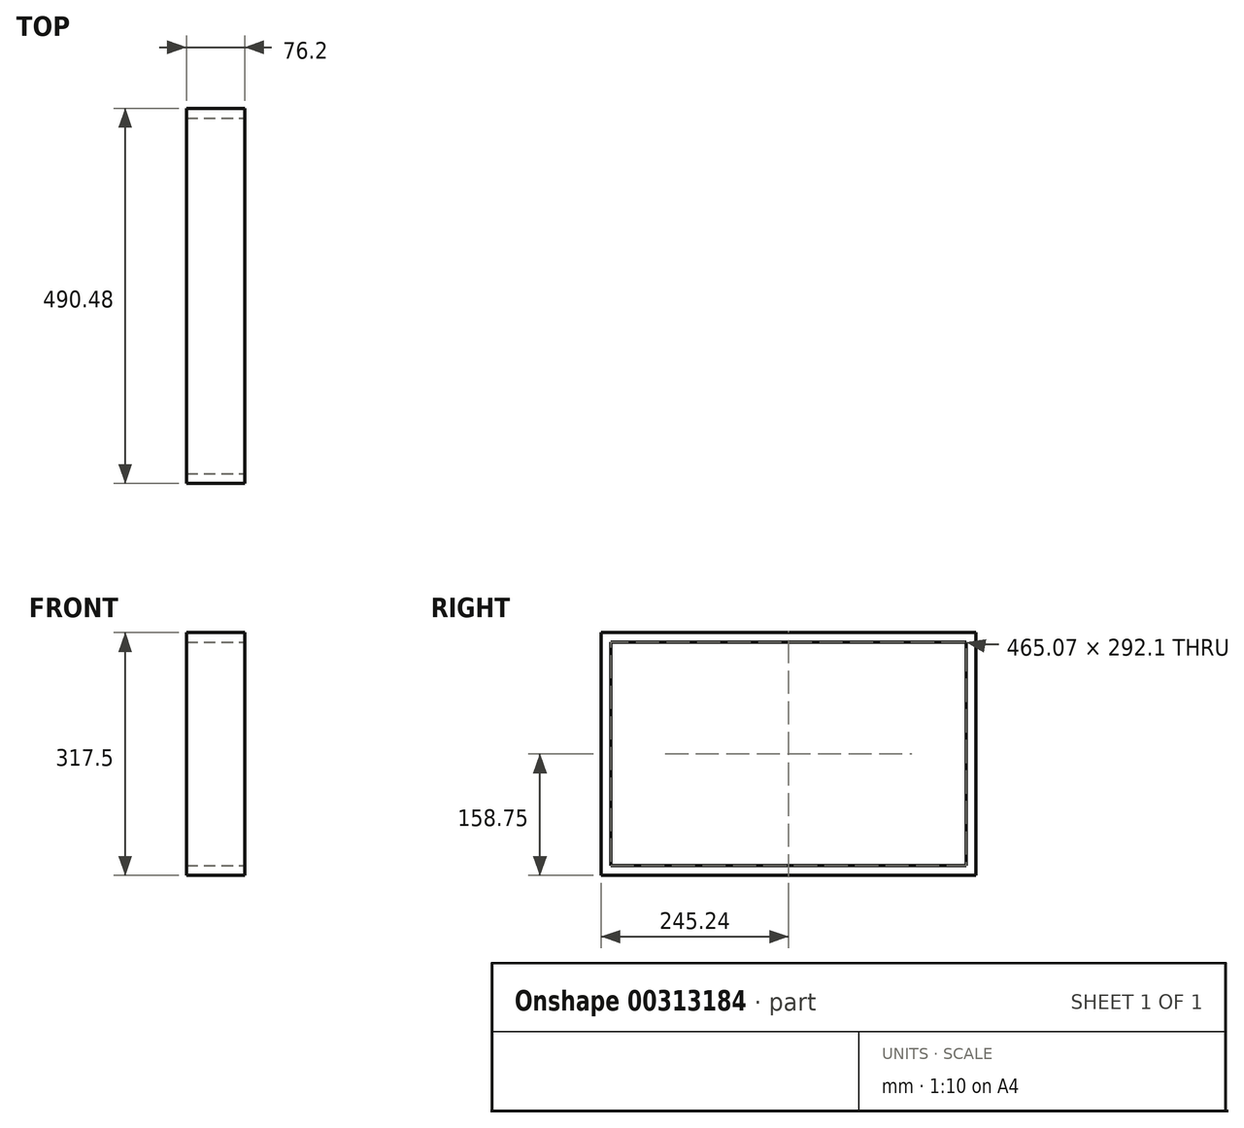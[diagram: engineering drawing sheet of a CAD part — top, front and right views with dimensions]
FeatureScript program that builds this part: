
annotation { "Feature Type Name" : "Feature", "Feature Type Description" : "" }
export const myFeature = defineFeature(function(context is Context, id is Id, definition is map)
    precondition{}
    {
        {
            var Q0;
            Q0=qCreatedBy(makeId("Right.planeOp"),FACE);
            var sketch = newSketch(context, id + "F0", { "sketchPlane" : qUnion([Q0])});
            skLineSegment(sketch, "E0.bottom", {"start": v(245.24, 158.75) * mm, "end": v(-245.24, 158.75) * mm});
            skLineSegment(sketch, "E0.top", {"start": v(245.24, -158.75) * mm, "end": v(-245.24, -158.75) * mm});
            skLineSegment(sketch, "E0.left", {"start": v(245.24, 158.75) * mm, "end": v(245.24, -158.75) * mm});
            skLineSegment(sketch, "E0.right", {"start": v(-245.24, 158.75) * mm, "end": v(-245.24, -158.75) * mm});
            skPoint(sketch, "E0.middle", {"position": v(0, 0) * mm});
            skLineSegment(sketch, "E1.bottom", {"start": v(232.54, 146.05) * mm, "end": v(-232.54, 146.05) * mm});
            skLineSegment(sketch, "E1.top", {"start": v(232.54, -146.05) * mm, "end": v(-232.54, -146.05) * mm});
            skLineSegment(sketch, "E1.left", {"start": v(232.54, 146.05) * mm, "end": v(232.54, -146.05) * mm});
            skLineSegment(sketch, "E1.right", {"start": v(-232.54, 146.05) * mm, "end": v(-232.54, -146.05) * mm});
            skPoint(sketch, "E2", {"position": v(-245.24, 158.75) * mm});
            skPoint(sketch, "E3", {"position": v(-207.14, 158.75) * mm});
            skPoint(sketch, "E4", {"position": v(-207.14, -158.75) * mm});
            skSolve(sketch);
        }
        {
            var Q0;
            Q0=makeQuery(id+"F0.imprint","IMPRINT",FACE,{"disambiguationData":[TD([[makeQuery(id+"F0.imprint","IMPRINT",EDGE,{"derivedFrom":sQuery(id+"F0.wireOp",EDGE,"E0.top")}),-1.0]])]});
            extrude(context, id + "F1", {"entities" : qUnion([Q0]), "endBound" : BoundingType.SYMMETRIC, "oppositeDirection" : true, "depth" : 76.2 * mm});
        }
        {
            var Q0;
            Q0=qCreatedBy(makeId("Top.planeOp"),FACE);
            var sketch = newSketch(context, id + "F2", { "sketchPlane" : qUnion([Q0])});
            skLineSegment(sketch, "E5", {"start": v(0, -245.41) * mm, "end": v(0, -207.31) * mm, "construction": true});
            skCircle(sketch, "E6", {"center": v(0, -207.31) * mm, "radius": 3.18 * mm});
            skSolve(sketch);
        }
        {
            var Q0;
            Q0=sQuery(id+"F2.wireOp",EDGE,"E6");
            extrude(context, id + "F3", {"bodyType" : ToolBodyType.SURFACE, "surfaceEntities" : qUnion([Q0]), "depth" : 158.75 * mm, "hasSecondDirection" : true, "secondDirectionOppositeDirection" : true, "secondDirectionDepth" : 158.75 * mm});
        }
    });
